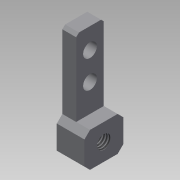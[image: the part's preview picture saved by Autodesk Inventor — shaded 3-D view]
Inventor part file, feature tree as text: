
AUTODESK INVENTOR PART (.ipt)
format: ipt  version: 2014 (Build 180170000, 170)  size: 137,728 bytes
history: native  units: mm
features: sketch x6, extrude x5, chamfer x2, hole x1
ambient origin geometry x8: Origin, YZ Plane, XZ Plane, XY Plane, X Axis, Y Axis, Z Axis, Center Point
bodies: Solid1 (feature_tree)
feature tree (14):
  extrude  "Extrusion1"  Depth=10.0mm TaperAngle=0.0deg
  extrude  "Extrusion2"  Depth=2.0mm TaperAngle=0.0deg
  extrude  "Extrusion3"  Depth=2.0mm TaperAngle=0.0deg
  extrude  "Extrusion4"  Depth=2.0mm
  sketch  "Sketch6"  dims[d25=30.0mm d26=5.0mm d27=0.0mm]
  chamfer  "Chamfer3"  Distance=5.0mm
  extrude  "Extrusion6"  Depth=10.0mm
  chamfer  "Chamfer4"  Distance=5.0mm
  hole  "Hole1"  [1 undecoded]
  sketch  "Sketch1"  dims[d0=5.0mm d1=0.0mm d2=10.0mm d3=0.0mm]
  sketch  "Sketch2"  dims[d5=12.5mm d6=2.0mm d7=0.0mm]
  sketch  "Sketch4"  dims[d8=12.5mm d9=2.0mm d10=0.0mm]
  sketch  "Sketch5"  dims[d20=1.0mm d21=2.0mm d22=45.0deg d23=30.0mm]
  sketch  "Sketch7"  dims[d28=2.0mm d29=2.0mm d30=45.0deg d31=4.917mm d32=6.0mm d33=4.0mm d34=2.0mm d35=90.0deg d36=8.0mm d37=20.594885mm d38=10.0mm d39=5.0mm d40=5.0mm d41=10.0mm d42=5.0mm d43=5.0mm d44=7.0mm d45=6.25mm]
note: 1 required parameter value undecoded (feature->parameter linkage not recoverable at this tier; creation-order binding heuristic only, values carry confidence <= 0.55)
